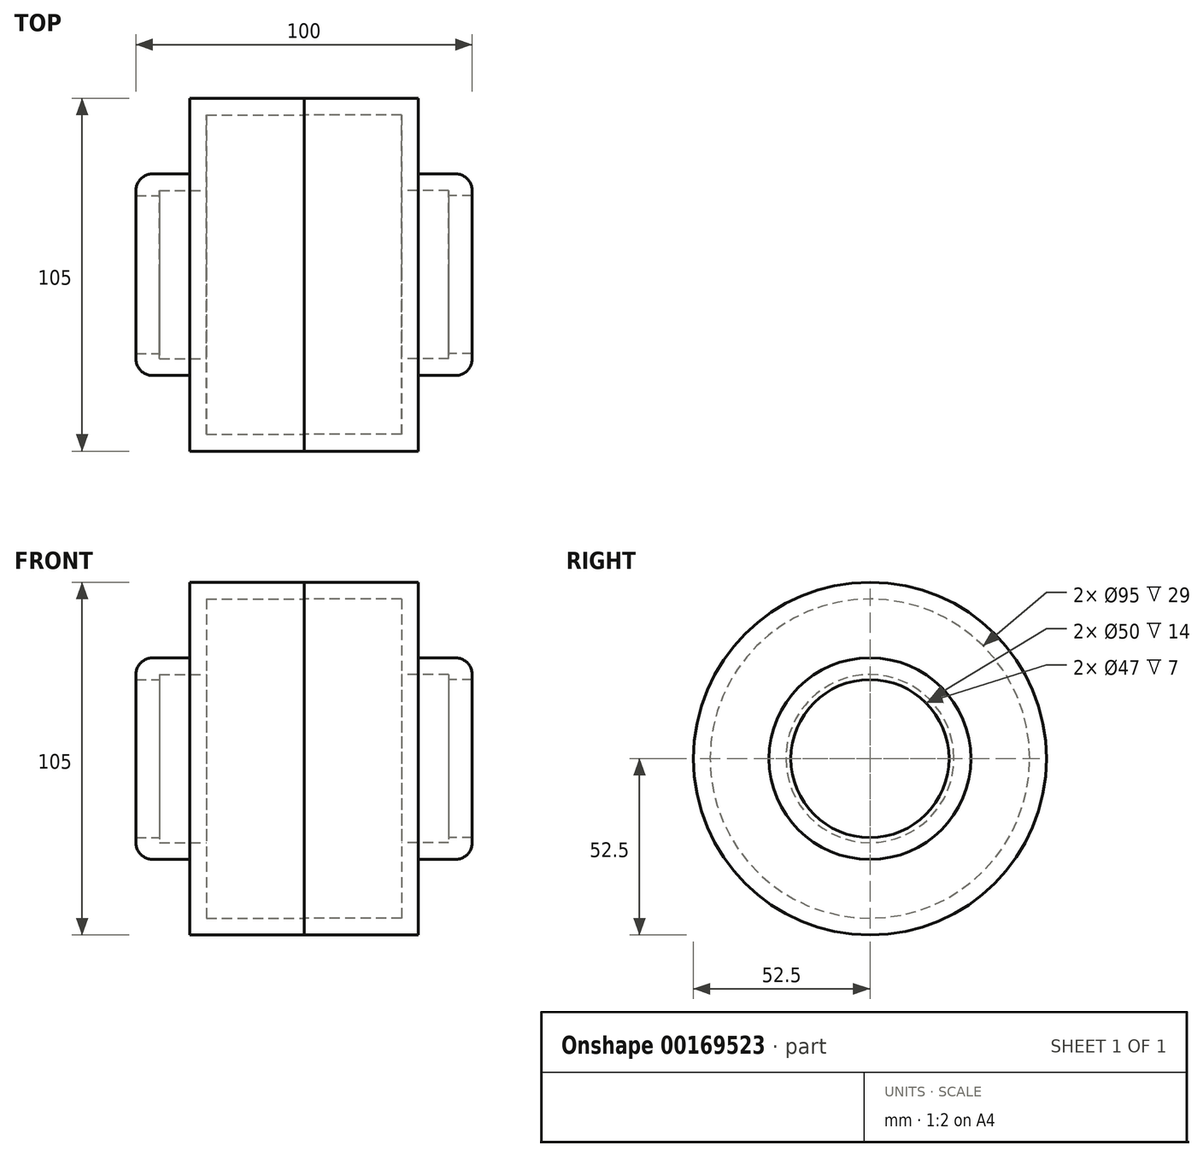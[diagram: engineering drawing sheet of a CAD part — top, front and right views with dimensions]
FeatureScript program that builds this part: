
annotation { "Feature Type Name" : "Feature", "Feature Type Description" : "" }
export const myFeature = defineFeature(function(context is Context, id is Id, definition is map)
    precondition{}
    {
        {
            var Q0;
            Q0=qCreatedBy(makeId("Front.planeOp"),FACE);
            var sketch = newSketch(context, id + "F0", { "sketchPlane" : qUnion([Q0])});
            skLineSegment(sketch, "E0", {"start": v(-62.91, 0) * mm, "end": v(64.01, 0) * mm, "construction": true});
            skLineSegment(sketch, "E1", {"start": v(0, 47.5) * mm, "end": v(29, 47.5) * mm});
            skLineSegment(sketch, "E2", {"start": v(29, 47.5) * mm, "end": v(29, 25) * mm});
            skLineSegment(sketch, "E3", {"start": v(34, 30) * mm, "end": v(34, 52.5) * mm});
            skLineSegment(sketch, "E4", {"start": v(34, 52.5) * mm, "end": v(0, 52.5) * mm});
            skLineSegment(sketch, "E5", {"start": v(0, 52.5) * mm, "end": v(0, 47.5) * mm});
            skLineSegment(sketch, "E6", {"start": v(29, 25) * mm, "end": v(43, 25) * mm});
            skLineSegment(sketch, "E7", {"start": v(43, 25) * mm, "end": v(43, 23.5) * mm});
            skLineSegment(sketch, "E8", {"start": v(43, 23.5) * mm, "end": v(50, 23.5) * mm});
            skLineSegment(sketch, "E9", {"start": v(50, 23.5) * mm, "end": v(50, 30) * mm});
            skLineSegment(sketch, "E10", {"start": v(50, 30) * mm, "end": v(34, 30) * mm});
            skSolve(sketch);
        }
        {
            var Q0;
            Q0 = qSketchRegion(id + "F0", true);
            var Q1;
            Q1=sQuery(id+"F0.wireOp",EDGE,"E0");
            revolve(context, id + "F1", {"entities" : qUnion([Q0]), "axis" : qUnion([Q1]), "revolveType" : RevolveType.FULL});
        }
        {
            var Q0;
            Q0=makeQuery(id+"F1.opRevolve","SWEPT_EDGE",EDGE,{"disambiguationData":[OSD([sQuery(id+"F0.wireOp",EDGE,"E9"),sQuery(id+"F0.wireOp",EDGE,"E10")])]});
            fillet(context, id + "F2", {"entities" : qUnion([Q0]), "radius" : 5 * mm, "tangentPropagation" : true, "allowEdgeOverflow" : false});
        }
        {
            var Q0;
            Q0=makeQuery(id+"F1.opRevolve","SWEPT_BODY",BODY,{"disambiguationData":[OSD([sQuery(id+"F0.wireOp",EDGE,"E1"),sQuery(id+"F0.wireOp",EDGE,"E2"),sQuery(id+"F0.wireOp",EDGE,"E3"),sQuery(id+"F0.wireOp",EDGE,"E4"),sQuery(id+"F0.wireOp",EDGE,"E5"),sQuery(id+"F0.wireOp",EDGE,"E6"),sQuery(id+"F0.wireOp",EDGE,"E7"),sQuery(id+"F0.wireOp",EDGE,"E8"),sQuery(id+"F0.wireOp",EDGE,"E9"),sQuery(id+"F0.wireOp",EDGE,"E10")])]});
            var Q1;
            Q1=qCreatedBy(makeId("Right.planeOp"),FACE);
            mirror(context, id + "F3", {"entities" : qUnion([Q0]), "mirrorPlane" : qUnion([Q1])});
        }
    });
